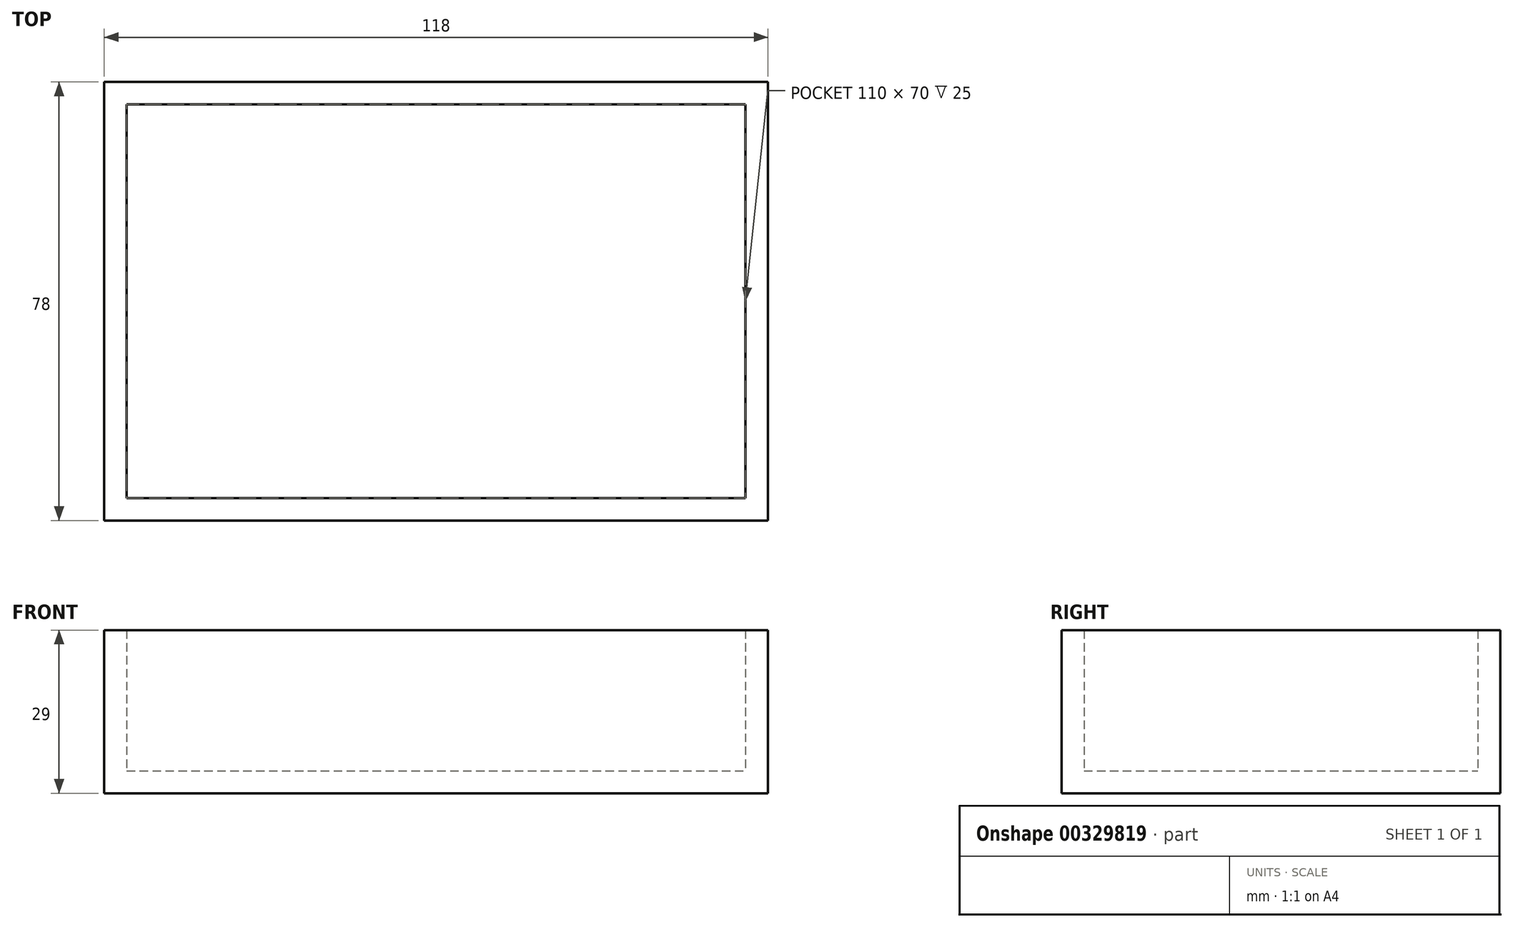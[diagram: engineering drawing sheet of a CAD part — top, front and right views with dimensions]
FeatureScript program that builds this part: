
annotation { "Feature Type Name" : "Feature", "Feature Type Description" : "" }
export const myFeature = defineFeature(function(context is Context, id is Id, definition is map)
    precondition{}
    {
        {
            var Q0;
            Q0=qCreatedBy(makeId("Top.planeOp"),FACE);
            var sketch = newSketch(context, id + "F0", { "sketchPlane" : qUnion([Q0])});
            skLineSegment(sketch, "E0.bottom", {"start": v(0, 0) * mm, "end": v(118, 0) * mm});
            skLineSegment(sketch, "E0.top", {"start": v(0, 78) * mm, "end": v(118, 78) * mm});
            skLineSegment(sketch, "E0.left", {"start": v(0, 0) * mm, "end": v(0, 78) * mm});
            skLineSegment(sketch, "E0.right", {"start": v(118, 0) * mm, "end": v(118, 78) * mm});
            skLineSegment(sketch, "E1.bottom", {"start": v(4, 4) * mm, "end": v(114, 4) * mm});
            skLineSegment(sketch, "E1.top", {"start": v(4, 74) * mm, "end": v(114, 74) * mm});
            skLineSegment(sketch, "E1.left", {"start": v(4, 4) * mm, "end": v(4, 74) * mm});
            skLineSegment(sketch, "E1.right", {"start": v(114, 4) * mm, "end": v(114, 74) * mm});
            skLineSegment(sketch, "E2", {"start": v(59, 74) * mm, "end": v(59, 78) * mm, "construction": true});
            skLineSegment(sketch, "E3", {"start": v(114, 39) * mm, "end": v(118, 39) * mm, "construction": true});
            skSolve(sketch);
        }
        {
            var Q0;
            Q0=makeQuery(id+"F0.imprint","IMPRINT",FACE,{"disambiguationData":[TD([[makeQuery(id+"F0.imprint","IMPRINT",EDGE,{"derivedFrom":sQuery(id+"F0.wireOp",EDGE,"E0.bottom")}),1.0]])]});
            extrude(context, id + "F1", {"entities" : qUnion([Q0]), "depth" : 25 * mm});
        }
        {
            var Q0;
            Q0=makeQuery(id+"F0.imprint","IMPRINT",FACE,{"disambiguationData":[TD([[makeQuery(id+"F0.imprint","IMPRINT",EDGE,{"derivedFrom":sQuery(id+"F0.wireOp",EDGE,"E0.bottom")}),1.0]])]});
            var Q1;
            Q1=makeQuery(id+"F0.imprint","IMPRINT",FACE,{"disambiguationData":[TD([[makeQuery(id+"F0.imprint","IMPRINT",EDGE,{"derivedFrom":sQuery(id+"F0.wireOp",EDGE,"E1.bottom")}),1.0]])]});
            extrude(context, id + "F2", {"entities" : qUnion([Q0, Q1]), "operationType" : NewBodyOperationType.ADD, "oppositeDirection" : true, "depth" : 4 * mm});
        }
    });
